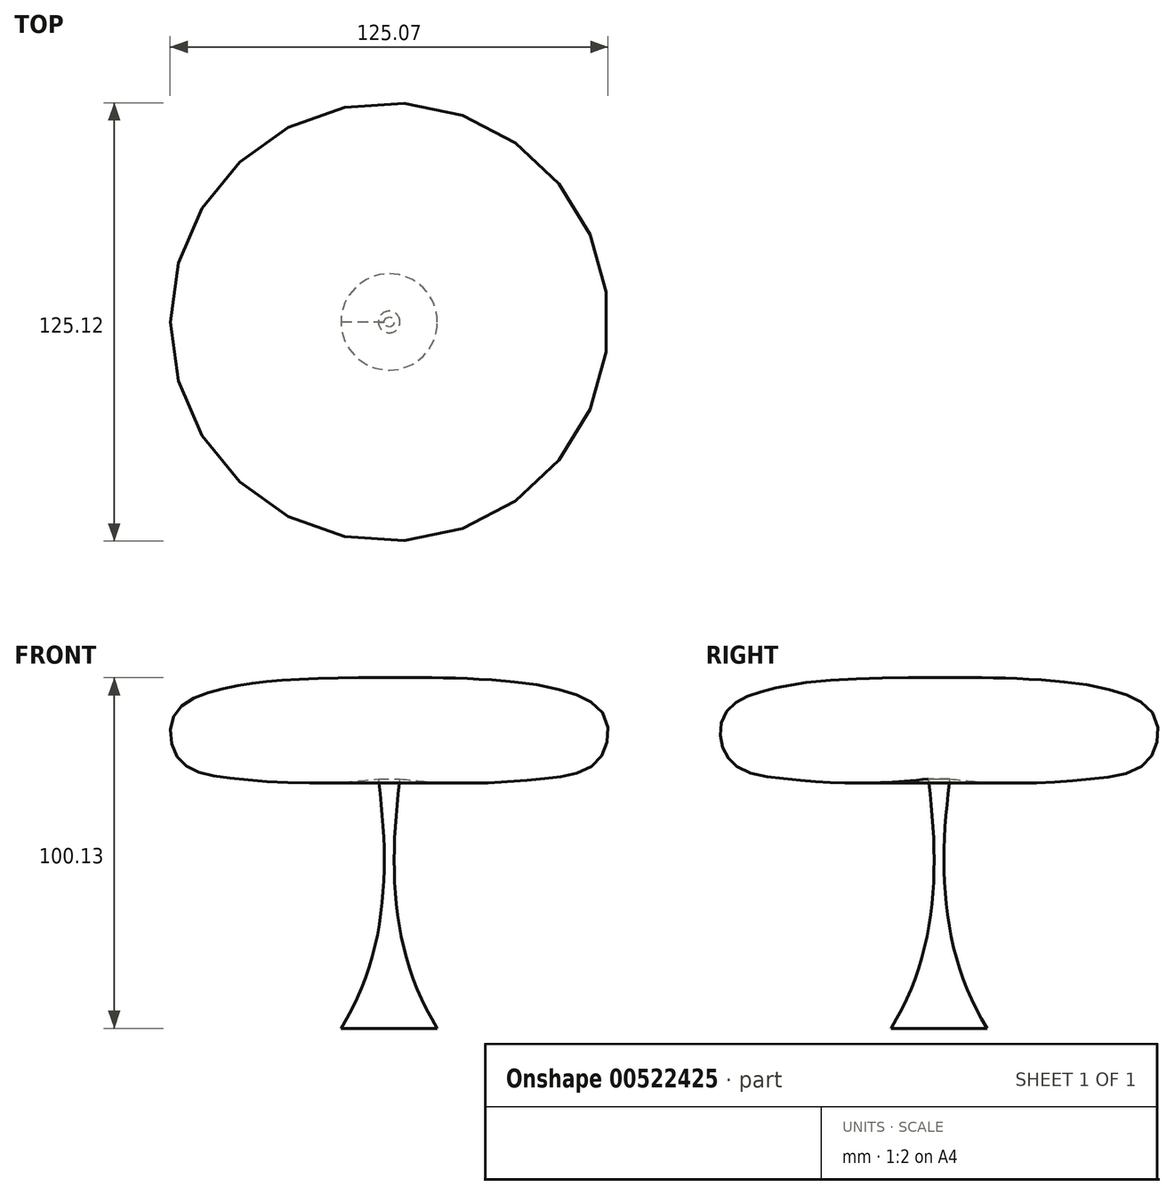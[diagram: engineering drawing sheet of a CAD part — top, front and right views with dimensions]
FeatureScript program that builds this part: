
annotation { "Feature Type Name" : "Feature", "Feature Type Description" : "" }
export const myFeature = defineFeature(function(context is Context, id is Id, definition is map)
    precondition{}
    {
        {
            var Q0;
            Q0=qCreatedBy(makeId("Front.planeOp"),FACE);
            var sketch = newSketch(context, id + "F0", { "sketchPlane" : qUnion([Q0])});
            skFitSpline(sketch, "E0", {"points": [v(0, 42.15) * mm, v(-30, 41.57) * mm, v(-47.02, 39.25) * mm, v(-61.34, 31.7) * mm, v(-59.6, 18.51) * mm, v(-43.15, 13.32) * mm, v(-3.1, 13.35) * mm], "startDerivative": vector(-162.02, 5.12) * mm, "endDerivative": vector(228.1, 26.83) * mm});
            skLineSegment(sketch, "E1", {"start": v(-13.74, -57.85) * mm, "end": v(0, -57.85) * mm});
            skLineSegment(sketch, "E2", {"start": v(0, -57.85) * mm, "end": v(0, 42.15) * mm});
            skFitSpline(sketch, "E3", {"points": [v(-3.1, 13.35) * mm, v(-13.74, -57.85) * mm], "startDerivative": vector(9.29, -70.82) * mm, "endDerivative": vector(-41.21, -65.6) * mm});
            skSolve(sketch);
        }
        {
            var Q0;
            Q0=makeQuery(id+"F0.imprint","IMPRINT",FACE,{"disambiguationData":[TD([[makeQuery(id+"F0.imprint","IMPRINT",EDGE,{"derivedFrom":sQuery(id+"F0.wireOp",EDGE,"E0")}),1.0]])]});
            var Q1;
            Q1=sQuery(id+"F0.wireOp",EDGE,"E2");
            revolve(context, id + "F1", {"entities" : qUnion([Q0]), "axis" : qUnion([Q1]), "revolveType" : RevolveType.FULL});
        }
    });
